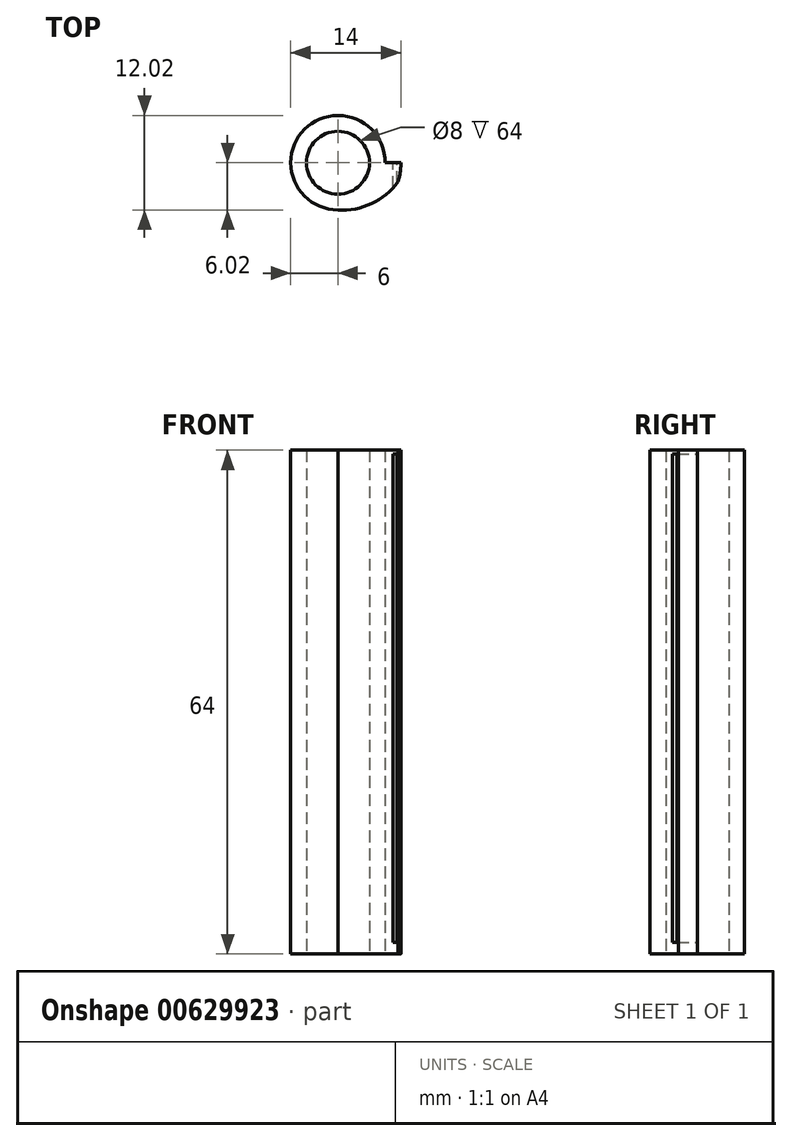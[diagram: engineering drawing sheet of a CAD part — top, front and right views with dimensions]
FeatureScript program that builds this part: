
annotation { "Feature Type Name" : "Feature", "Feature Type Description" : "" }
export const myFeature = defineFeature(function(context is Context, id is Id, definition is map)
    precondition{}
    {
        {
            var Q0;
            Q0=qCreatedBy(makeId("Top.planeOp"),FACE);
            var sketch = newSketch(context, id + "F0", { "sketchPlane" : qUnion([Q0])});
            skCircle(sketch, "E0", {"center": v(0, 0) * mm, "radius": 4 * mm});
            skCircle(sketch, "E1.0", {"center": v(0, 0) * mm, "radius": 6 * mm});
            skArc(sketch, "E2", {"start": v(7.63, -2.42) * mm, "mid": v(7.9, -1.22) * mm, "end": v(8, 0) * mm});
            skArc(sketch, "E3", {"start": v(0, -6) * mm, "mid": v(4.27, -5.19) * mm, "end": v(7.63, -2.42) * mm});
            skLineSegment(sketch, "E4", {"start": v(8, 0) * mm, "end": v(6, 0) * mm});
            skSolve(sketch);
        }
        {
            var Q0;
            Q0=makeQuery(id+"F0.imprint","IMPRINT",FACE,{"disambiguationData":[TD([[makeQuery(id+"F0.imprint","IMPRINT",EDGE,{"derivedFrom":sQuery(id+"F0.wireOp",EDGE,"E0")}),-1.0]])]});
            extrude(context, id + "F1", {"entities" : qUnion([Q0]), "depth" : 64 * mm, "offsetDistance" : 25 * mm});
        }
        {
            var Q0;
            Q0=makeQuery(id+"F0.imprint","IMPRINT",FACE,{"disambiguationData":[TD([[makeQuery(id+"F0.imprint","IMPRINT",EDGE,{"derivedFrom":sQuery(id+"F0.wireOp",EDGE,"E2")}),1.0]])]});
            extrude(context, id + "F2", {"entities" : qUnion([Q0]), "operationType" : NewBodyOperationType.ADD, "depth" : 64 * mm, "offsetDistance" : 25 * mm});
        }
        {
            var Q0;
            Q0=makeQuery(id+"F2.opExtrude","SWEPT_FACE",FACE,{"disambiguationData":[OSD([sQuery(id+"F0.wireOp",EDGE,"E4")])]});
            var sketch = newSketch(context, id + "F3", { "sketchPlane" : qUnion([Q0])});
            skPoint(sketch, "E5.oppositeSnap0", {"position": v(-7, 0) * mm});
            skLineSegment(sketch, "E5.bottom", {"start": v(-7.5, 63.5) * mm, "end": v(-7, 63.5) * mm});
            skLineSegment(sketch, "E5.top", {"start": v(-7.5, 1.5) * mm, "end": v(-7, 1.5) * mm});
            skLineSegment(sketch, "E5.left", {"start": v(-7.5, 63.5) * mm, "end": v(-7.5, 1.5) * mm});
            skLineSegment(sketch, "E5.right", {"start": v(-7, 63.5) * mm, "end": v(-7, 1.5) * mm});
            skSolve(sketch);
        }
        {
            var Q0;
            Q0=makeQuery(id+"F3.imprint","IMPRINT",FACE,{"disambiguationData":[TD([[makeQuery(id+"F3.imprint","IMPRINT",EDGE,{"derivedFrom":sQuery(id+"F3.wireOp",EDGE,"E5.bottom")}),-1.0]])]});
            extrude(context, id + "F4", {"entities" : qUnion([Q0]), "operationType" : NewBodyOperationType.REMOVE, "oppositeDirection" : true, "depth" : 25 * mm, "offsetDistance" : 25 * mm});
        }
    });
